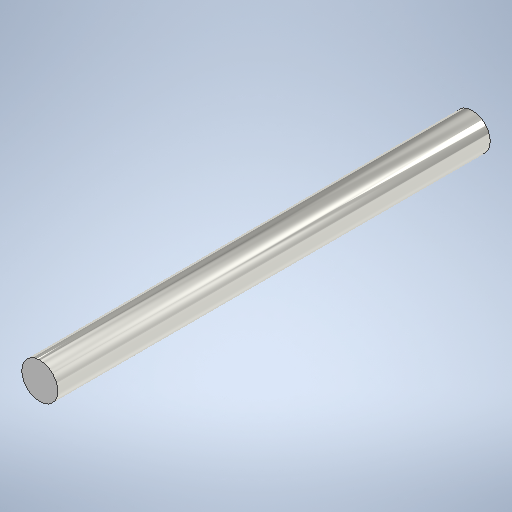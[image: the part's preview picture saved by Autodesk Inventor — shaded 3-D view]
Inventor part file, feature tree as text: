
AUTODESK INVENTOR PART (.ipt)
format: ipt  version: 2025 (Build 290162000, 162)  size: 268,800 bytes
history: native  units: in
note: dims shown in document units (in); Inventor stores cm internally (conversion verified against a paired STEP export)
features: extrude x1, sketch x1
ambient origin geometry x8: Origin, YZ Plane, XZ Plane, XY Plane, X Axis, Y Axis, Z Axis, Center Point
bodies: Solid1 (feature_tree)
feature tree (2):
  extrude  "Extrusion1"  Depth=4.7244in TaperAngle=0.0deg
  sketch  "Sketch1"  dims[d0=0.3937in d1=4.7244in d2=0.0in]
